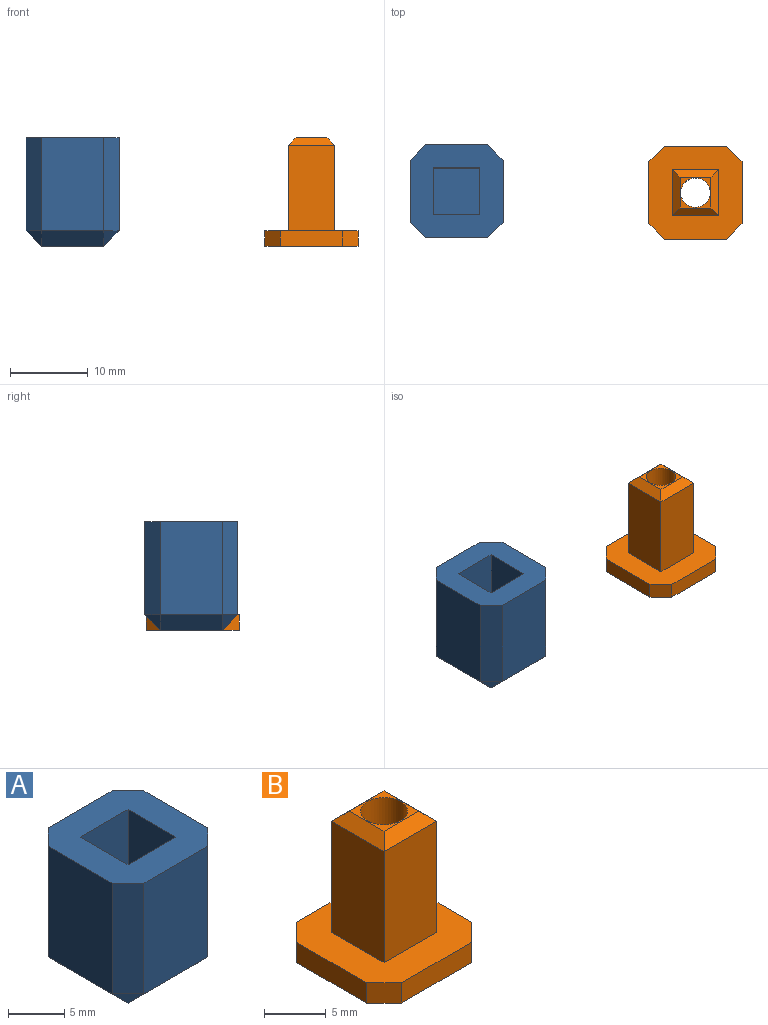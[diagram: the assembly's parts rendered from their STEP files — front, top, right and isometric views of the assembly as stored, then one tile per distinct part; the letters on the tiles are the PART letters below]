
ASSEMBLY  parts=2 mates=1
PART A: 23 faces, bbox 12x12x14 mm
  f0: plane 12x8mm, normal (0,1,0), area 96mm2, adj f9,f11,f15,f16
  f1: plane 12x8mm, normal (-1,0,0), area 96mm2, adj f9,f16,f20,f22
  f2: plane 12x8mm, normal (0,-1,0), area 96mm2, adj f9,f13,f19,f22
  f3: plane 12x8mm, normal (1,0,0), area 96mm2, adj f9,f11,f13,f14
  f4: plane 8x8mm, normal (0,0,-1), area 64mm2, adj f14,f15,f19,f20
  f5: plane 12x6mm, normal (1,0,0), area 72mm2, adj f6,f8,f9,f10
  f6: plane 12x6mm, normal (0,-1,0), area 72mm2, adj f5,f7,f9,f10
  f7: plane 12x6mm, normal (-1,0,0), area 72mm2, adj f6,f8,f9,f10
  f8: plane 12x6mm, normal (0,1,0), area 72mm2, adj f5,f7,f9,f10
  f9: plane 12x12mm, normal (0,0,1), area 100mm2, adj f0,f1,f2,f3,f5,f6,f7,f8
  f10: plane 6x6mm, normal (0,0,1), area 36mm2, adj f5,f6,f7,f8
  f11: plane 12x2mm, normal (0.71,0.71,0), area 33.9mm2, adj f0,f3,f9,f12
  f12: plane 2x2mm, normal (0.58,0.58,-0.58), area 3.5mm2, adj f11,f14,f15
  f13: plane 12x2mm, normal (0.71,-0.71,0), area 33.9mm2, adj f2,f3,f9,f17
  f14: plane 8x2mm, normal (0.71,0,-0.71), area 22.6mm2, adj f3,f4,f12,f17
  f15: plane 8x2mm, normal (0,0.71,-0.71), area 22.6mm2, adj f0,f4,f12,f18
  f16: plane 12x2mm, normal (-0.71,0.71,0), area 33.9mm2, adj f0,f1,f9,f18
  f17: plane 2x2mm, normal (0.58,-0.58,-0.58), area 3.5mm2, adj f13,f14,f19
  f18: plane 2x2mm, normal (-0.58,0.58,-0.58), area 3.5mm2, adj f15,f16,f20
  f19: plane 8x2mm, normal (0,-0.71,-0.71), area 22.6mm2, adj f2,f4,f17,f21
  f20: plane 8x2mm, normal (-0.71,0,-0.71), area 22.6mm2, adj f1,f4,f18,f21
  f21: plane 2x2mm, normal (-0.58,-0.58,-0.58), area 3.5mm2, adj f19,f20,f22
  f22: plane 12x2mm, normal (-0.71,-0.71,0), area 33.9mm2, adj f1,f2,f9,f21
PART B: 20 faces, bbox 12x12x14 mm
  f0: plane 12x12mm, normal (0,0,1), area 100.2mm2, adj f1,f2,f3,f4,f7,f8,f9,f10
  f1: plane 8x2mm, normal (0,1,0), area 16mm2, adj f0,f6,f12,f15
  f2: plane 8x2mm, normal (-1,0,0), area 16mm2, adj f0,f6,f14,f15
  f3: plane 8x2mm, normal (0,-1,0), area 16mm2, adj f0,f6,f13,f14
  f4: plane 8x2mm, normal (1,0,0), area 16mm2, adj f0,f6,f12,f13
  f5: cylinder r=1.9mm len=14mm, axis (0,0,1), area 167.1mm2, adj f6,f11
  f6: plane 12x12mm, normal (0,0,-1), area 124.7mm2, adj f1,f2,f3,f4,f5,f12,f13,f14
  f7: plane 11x5.98mm, normal (0,1,0), area 65.8mm2, adj f0,f8,f10,f16
  f8: plane 11x5.98mm, normal (-1,0,0), area 65.8mm2, adj f0,f7,f9,f17
  f9: plane 11x5.98mm, normal (0,-1,0), area 65.8mm2, adj f0,f8,f10,f19
  f10: plane 11x5.98mm, normal (1,0,0), area 65.8mm2, adj f0,f7,f9,f18
  f11: plane 3.98x3.98mm, normal (0,0,1), area 4.5mm2, adj f5,f16,f17,f18,f19
  f12: plane 2x2mm, normal (0.71,0.71,0), area 5.7mm2, adj f0,f1,f4,f6
  f13: plane 2x2mm, normal (0.71,-0.71,0), area 5.7mm2, adj f0,f3,f4,f6
  f14: plane 2x2mm, normal (-0.71,-0.71,0), area 5.7mm2, adj f0,f2,f3,f6
  f15: plane 2x2mm, normal (-0.71,0.71,0), area 5.7mm2, adj f0,f1,f2,f6
  f16: plane 5.98x1mm, normal (0,0.71,0.71), area 7mm2, adj f7,f11,f17,f18
  f17: plane 5.98x1mm, normal (-0.71,0,0.71), area 7mm2, adj f8,f11,f16,f19
  f18: plane 5.98x1mm, normal (0.71,0,0.71), area 7mm2, adj f10,f11,f16,f19
  f19: plane 5.98x1mm, normal (0,-0.71,0.71), area 7mm2, adj f9,f11,f17,f18
PLACE A t=(-15.03,-0.13,-23.25)mm
PLACE B t=(15.77,-0.3,1.75)mm
MATE planar B.f5 <-> A.f4  axis (0,0,-1) through (15.77,-0.3,-0.25)mm
